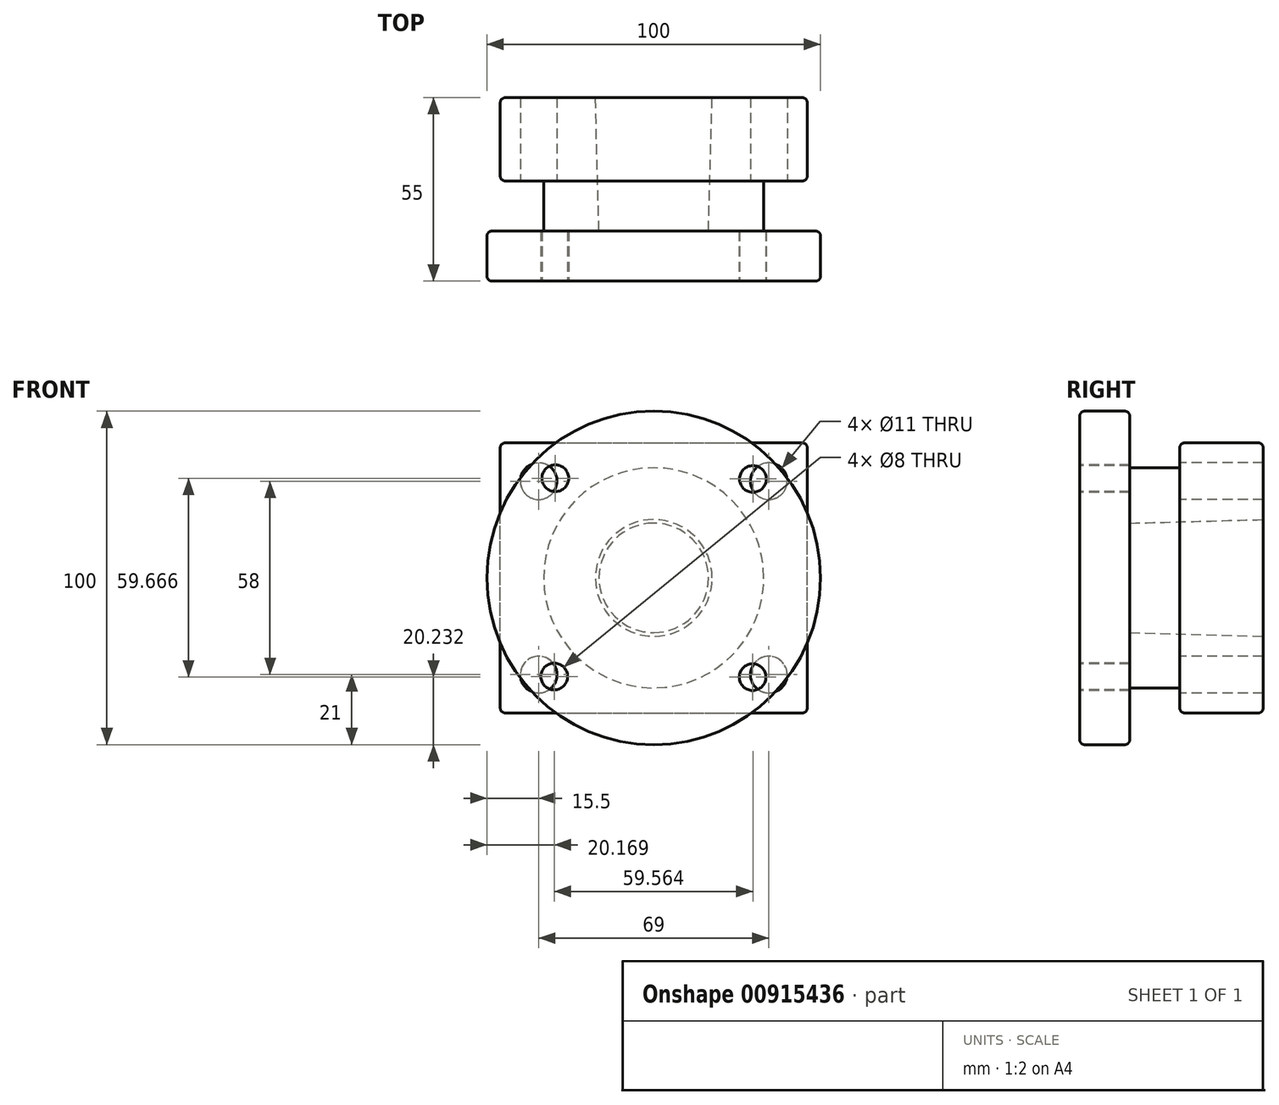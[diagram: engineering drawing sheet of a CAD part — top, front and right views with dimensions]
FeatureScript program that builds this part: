
annotation { "Feature Type Name" : "Feature", "Feature Type Description" : "" }
export const myFeature = defineFeature(function(context is Context, id is Id, definition is map)
    precondition{}
    {
        {
            var Q0;
            Q0=qCreatedBy(makeId("Front.planeOp"),FACE);
            var sketch = newSketch(context, id + "F0", { "sketchPlane" : qUnion([Q0])});
            skLineSegment(sketch, "E0.bottom", {"start": v(-46, -40.5) * mm, "end": v(46, -40.5) * mm});
            skLineSegment(sketch, "E0.top", {"start": v(-46, 40.5) * mm, "end": v(46, 40.5) * mm});
            skLineSegment(sketch, "E0.left", {"start": v(-46, -40.5) * mm, "end": v(-46, 40.5) * mm});
            skLineSegment(sketch, "E0.right", {"start": v(46, -40.5) * mm, "end": v(46, 40.5) * mm});
            skPoint(sketch, "E0.middle", {"position": v(0, 0) * mm});
            skCircle(sketch, "E1", {"center": v(-34.5, 29) * mm, "radius": 5.5 * mm});
            skCircle(sketch, "E2", {"center": v(-34.5, -29) * mm, "radius": 5.5 * mm});
            skLineSegment(sketch, "E3", {"start": v(0, 40.5) * mm, "end": v(0, -40.5) * mm, "construction": true});
            skCircle(sketch, "E4.MirrorC", {"center": v(34.5, 29) * mm, "radius": 5.5 * mm});
            skCircle(sketch, "E5.MirrorC", {"center": v(34.5, -29) * mm, "radius": 5.5 * mm});
            skSolve(sketch);
        }
        {
            var Q0;
            Q0 = qSketchRegion(id + "F0", true);
            extrude(context, id + "F1", {"entities" : qUnion([Q0]), "oppositeDirection" : true, "depth" : 25 * mm, "offsetDistance" : 25 * mm});
        }
        {
            var Q0;
            Q0=makeQuery(id+"F1.opExtrude","CAP_FACE",FACE,{"disambiguationData":[OSD([sQuery(id+"F0.wireOp",EDGE,"E0.bottom"),sQuery(id+"F0.wireOp",EDGE,"E0.top"),sQuery(id+"F0.wireOp",EDGE,"E0.left"),sQuery(id+"F0.wireOp",EDGE,"E0.right"),sQuery(id+"F0.wireOp",EDGE,"E1"),sQuery(id+"F0.wireOp",EDGE,"E2"),sQuery(id+"F0.wireOp",EDGE,"E4.MirrorC"),sQuery(id+"F0.wireOp",EDGE,"E5.MirrorC")])],"isStart":false});
            var sketch = newSketch(context, id + "F2", { "sketchPlane" : qUnion([Q0])});
            skCircle(sketch, "E6", {"center": v(0, 0) * mm, "radius": 33 * mm});
            skSolve(sketch);
        }
        {
            var Q0;
            Q0=makeQuery(id+"F1.opExtrude","CAP_FACE",FACE,{"disambiguationData":[OSD([sQuery(id+"F0.wireOp",EDGE,"E0.bottom"),sQuery(id+"F0.wireOp",EDGE,"E0.top"),sQuery(id+"F0.wireOp",EDGE,"E0.left"),sQuery(id+"F0.wireOp",EDGE,"E0.right"),sQuery(id+"F0.wireOp",EDGE,"E1"),sQuery(id+"F0.wireOp",EDGE,"E2"),sQuery(id+"F0.wireOp",EDGE,"E4.MirrorC"),sQuery(id+"F0.wireOp",EDGE,"E5.MirrorC")])],"isStart":true});
            var sketch = newSketch(context, id + "F3", { "sketchPlane" : qUnion([Q0])});
            skSolve(sketch);
        }
        {
            var Q0;
            Q0=makeQuery(id+"F3.imprint","IMPRINT",FACE,{"disambiguationData":[TD([[makeQuery(id+"F3.imprint","IMPRINT",EDGE,{"derivedFrom":makeQuery(id+"F1.opExtrude","CAP_EDGE",EDGE,{"disambiguationData":[OSD([sQuery(id+"F0.wireOp",EDGE,"E0.bottom")])],"isStart":true})}),1.0]])]});
            var sketch = newSketch(context, id + "F4", { "sketchPlane" : qUnion([Q0])});
            skCircle(sketch, "E7", {"center": v(0, 0) * mm, "radius": 33 * mm});
            skSolve(sketch);
        }
        {
            var Q1;
            Q1=makeQuery(id+"F2.imprint","IMPRINT",FACE,{"disambiguationData":[TD([[makeQuery(id+"F2.imprint","IMPRINT",EDGE,{"derivedFrom":sQuery(id+"F2.wireOp",EDGE,"E6")}),1.0]])]});
            var Q2;
            Q2=makeQuery(id+"F4.imprint","IMPRINT",FACE,{"disambiguationData":[TD([[makeQuery(id+"F4.imprint","IMPRINT",EDGE,{"derivedFrom":sQuery(id+"F4.wireOp",EDGE,"E7")}),1.0]])]});
            loft(context, id + "F5", {"operationType" : NewBodyOperationType.REMOVE, "sheetProfilesArray" : [{ "sheetProfileEntities" : qUnion([Q1]) }, { "sheetProfileEntities" : qUnion([Q2]) }]});
        }
        {
            var Q0;
            Q0=makeQuery(id+"F1.opExtrude","CAP_FACE",FACE,{"disambiguationData":[OSD([sQuery(id+"F0.wireOp",EDGE,"E0.bottom"),sQuery(id+"F0.wireOp",EDGE,"E0.top"),sQuery(id+"F0.wireOp",EDGE,"E0.left"),sQuery(id+"F0.wireOp",EDGE,"E0.right"),sQuery(id+"F0.wireOp",EDGE,"E1"),sQuery(id+"F0.wireOp",EDGE,"E2"),sQuery(id+"F0.wireOp",EDGE,"E4.MirrorC"),sQuery(id+"F0.wireOp",EDGE,"E5.MirrorC")])],"isStart":false});
            var sketch = newSketch(context, id + "F6", { "sketchPlane" : qUnion([Q0])});
            skCircle(sketch, "E8", {"center": v(0, 0) * mm, "radius": 33 * mm});
            skSolve(sketch);
        }
        {
            var Q0;
            Q0 = qSketchRegion(id + "F6", true);
            extrude(context, id + "F7", {"entities" : qUnion([Q0]), "operationType" : NewBodyOperationType.ADD, "oppositeDirection" : true, "depth" : 55 * mm, "offsetDistance" : 25 * mm});
        }
        {
            var Q0;
            Q0=makeQuery(id+"F7.opExtrude","CAP_FACE",FACE,{"disambiguationData":[OSD([sQuery(id+"F6.wireOp",EDGE,"E8")])],"isStart":false});
            var sketch = newSketch(context, id + "F8", { "sketchPlane" : qUnion([Q0])});
            skCircle(sketch, "E9", {"center": v(0, 0) * mm, "radius": 16 * mm});
            skSolve(sketch);
        }
        {
            var Q0;
            Q0=makeQuery(id+"F7.boolean.opBoolean","MERGE",FACE,{"derivedFrom":[makeQuery(id+"F1.opExtrude","CAP_FACE",FACE,{"disambiguationData":[OSD([sQuery(id+"F0.wireOp",EDGE,"E0.bottom"),sQuery(id+"F0.wireOp",EDGE,"E0.top"),sQuery(id+"F0.wireOp",EDGE,"E0.left"),sQuery(id+"F0.wireOp",EDGE,"E0.right"),sQuery(id+"F0.wireOp",EDGE,"E1"),sQuery(id+"F0.wireOp",EDGE,"E2"),sQuery(id+"F0.wireOp",EDGE,"E4.MirrorC"),sQuery(id+"F0.wireOp",EDGE,"E5.MirrorC")])],"isStart":false}),makeQuery(id+"F7.opExtrude","CAP_FACE",FACE,{"disambiguationData":[OSD([sQuery(id+"F6.wireOp",EDGE,"E8")])],"isStart":true})]});
            var sketch = newSketch(context, id + "F9", { "sketchPlane" : qUnion([Q0])});
            skCircle(sketch, "E10", {"center": v(0, 0) * mm, "radius": 17.5 * mm});
            skSolve(sketch);
        }
        {
            var Q1;
            Q1=makeQuery(id+"F9.imprint","IMPRINT",FACE,{"disambiguationData":[TD([[makeQuery(id+"F9.imprint","IMPRINT",EDGE,{"derivedFrom":sQuery(id+"F9.wireOp",EDGE,"E10")}),1.0]])]});
            var Q2;
            Q2=makeQuery(id+"F8.imprint","IMPRINT",FACE,{"disambiguationData":[TD([[makeQuery(id+"F8.imprint","IMPRINT",EDGE,{"derivedFrom":sQuery(id+"F8.wireOp",EDGE,"E9")}),1.0]])]});
            loft(context, id + "F10", {"operationType" : NewBodyOperationType.REMOVE, "sheetProfilesArray" : [{ "sheetProfileEntities" : qUnion([Q1]) }, { "sheetProfileEntities" : qUnion([Q2]) }]});
        }
        {
            var Q0;
            Q0=makeQuery(id+"F7.opExtrude","CAP_FACE",FACE,{"disambiguationData":[OSD([sQuery(id+"F6.wireOp",EDGE,"E8")])],"isStart":false});
            var sketch = newSketch(context, id + "F11", { "sketchPlane" : qUnion([Q0])});
            skCircle(sketch, "E11", {"center": v(0, 0) * mm, "radius": 50 * mm});
            skSolve(sketch);
        }
        {
            var Q0;
            Q0 = qSketchRegion(id + "F11", true);
            extrude(context, id + "F12", {"entities" : qUnion([Q0]), "operationType" : NewBodyOperationType.ADD, "oppositeDirection" : true, "depth" : 15 * mm, "offsetDistance" : 25 * mm});
        }
        {
            var Q0;
            Q0=makeQuery(id+"F12.boolean.opBoolean","MERGE",FACE,{"derivedFrom":[makeQuery(id+"F7.opExtrude","CAP_FACE",FACE,{"disambiguationData":[OSD([sQuery(id+"F6.wireOp",EDGE,"E8")])],"isStart":false}),makeQuery(id+"F12.opExtrude","CAP_FACE",FACE,{"disambiguationData":[OSD([sQuery(id+"F11.wireOp",EDGE,"E11")])],"isStart":true})]});
            var sketch = newSketch(context, id + "F13", { "sketchPlane" : qUnion([Q0])});
            skCircle(sketch, "E12", {"center": v(-29.5, 29.9) * mm, "radius": 4 * mm});
            skCircle(sketch, "E13", {"center": v(29.73, 29.66) * mm, "radius": 4 * mm});
            skCircle(sketch, "E14", {"center": v(-29.83, -29.57) * mm, "radius": 4 * mm});
            skCircle(sketch, "E15", {"center": v(29.63, -29.77) * mm, "radius": 4 * mm});
            skSolve(sketch);
        }
        {
            var Q0;
            Q0 = qSketchRegion(id + "F13", true);
            extrude(context, id + "F14", {"entities" : qUnion([Q0]), "operationType" : NewBodyOperationType.REMOVE, "oppositeDirection" : true, "depth" : 25 * mm, "offsetDistance" : 25 * mm});
        }
        {
            var Q0;
            Q0=makeQuery(id+"F1.opExtrude","CAP_EDGE",EDGE,{"disambiguationData":[OSD([sQuery(id+"F0.wireOp",EDGE,"E0.right")])],"isStart":false});
            var Q1;
            Q1=makeQuery(id+"F1.opExtrude","CAP_EDGE",EDGE,{"disambiguationData":[OSD([sQuery(id+"F0.wireOp",EDGE,"E0.top")])],"isStart":false});
            var Q2;
            Q2=makeQuery(id+"F1.opExtrude","SWEPT_EDGE",EDGE,{"disambiguationData":[OSD([sQuery(id+"F0.wireOp",EDGE,"E0.top"),sQuery(id+"F0.wireOp",EDGE,"E0.right")])]});
            var Q3;
            Q3=makeQuery(id+"F1.opExtrude","CAP_EDGE",EDGE,{"disambiguationData":[OSD([sQuery(id+"F0.wireOp",EDGE,"E0.right")])],"isStart":true});
            var Q4;
            Q4=makeQuery(id+"F1.opExtrude","CAP_EDGE",EDGE,{"disambiguationData":[OSD([sQuery(id+"F0.wireOp",EDGE,"E0.top")])],"isStart":true});
            var Q5;
            Q5=makeQuery(id+"F1.opExtrude","SWEPT_EDGE",EDGE,{"disambiguationData":[OSD([sQuery(id+"F0.wireOp",EDGE,"E0.bottom"),sQuery(id+"F0.wireOp",EDGE,"E0.right")])]});
            var Q6;
            Q6=makeQuery(id+"F1.opExtrude","SWEPT_EDGE",EDGE,{"disambiguationData":[OSD([sQuery(id+"F0.wireOp",EDGE,"E0.top"),sQuery(id+"F0.wireOp",EDGE,"E0.left")])]});
            var Q7;
            Q7=makeQuery(id+"F1.opExtrude","CAP_EDGE",EDGE,{"disambiguationData":[OSD([sQuery(id+"F0.wireOp",EDGE,"E0.left")])],"isStart":false});
            var Q8;
            Q8=makeQuery(id+"F1.opExtrude","CAP_EDGE",EDGE,{"disambiguationData":[OSD([sQuery(id+"F0.wireOp",EDGE,"E0.left")])],"isStart":true});
            var Q9;
            Q9=makeQuery(id+"F1.opExtrude","SWEPT_EDGE",EDGE,{"disambiguationData":[OSD([sQuery(id+"F0.wireOp",EDGE,"E0.bottom"),sQuery(id+"F0.wireOp",EDGE,"E0.left")])]});
            var Q10;
            Q10=makeQuery(id+"F12.opExtrude","CAP_EDGE",EDGE,{"disambiguationData":[OSD([sQuery(id+"F11.wireOp",EDGE,"E11")])],"isStart":true});
            var Q11;
            Q11=makeQuery(id+"F12.opExtrude","CAP_EDGE",EDGE,{"disambiguationData":[OSD([sQuery(id+"F11.wireOp",EDGE,"E11")])],"isStart":false});
            var Q12;
            Q12=makeQuery(id+"F1.opExtrude","CAP_EDGE",EDGE,{"disambiguationData":[OSD([sQuery(id+"F0.wireOp",EDGE,"E0.bottom")])],"isStart":true});
            var Q13;
            Q13=makeQuery(id+"F1.opExtrude","CAP_EDGE",EDGE,{"disambiguationData":[OSD([sQuery(id+"F0.wireOp",EDGE,"E0.bottom")])],"isStart":false});
            var Q14;
            Q14=makeQuery(id+"F5.boolean.opBoolean","COPY",EDGE,{"derivedFrom":makeQuery(id+"F5.opLoft","MID_CAP_EDGE",EDGE,{"disambiguationData":[OSD([sQuery(id+"F4.wireOp",EDGE,"E7")])],"capPos":1.0})});
            var Q15;
            Q15=makeQuery(id+"F10.boolean.opBoolean","COPY",EDGE,{"derivedFrom":makeQuery(id+"F10.opLoft","MID_CAP_EDGE",EDGE,{"disambiguationData":[OSD([sQuery(id+"F9.wireOp",EDGE,"E10")])],"capPos":0.0})});
            fillet(context, id + "F15", {"entities" : qUnion([Q0, Q1, Q2, Q3, Q4, Q5, Q6, Q7, Q8, Q9, Q10, Q11, Q12, Q13, Q14, Q15]), "radius" : 1.5 * mm, "tangentPropagation" : true, "allowEdgeOverflow" : false});
        }
    });
